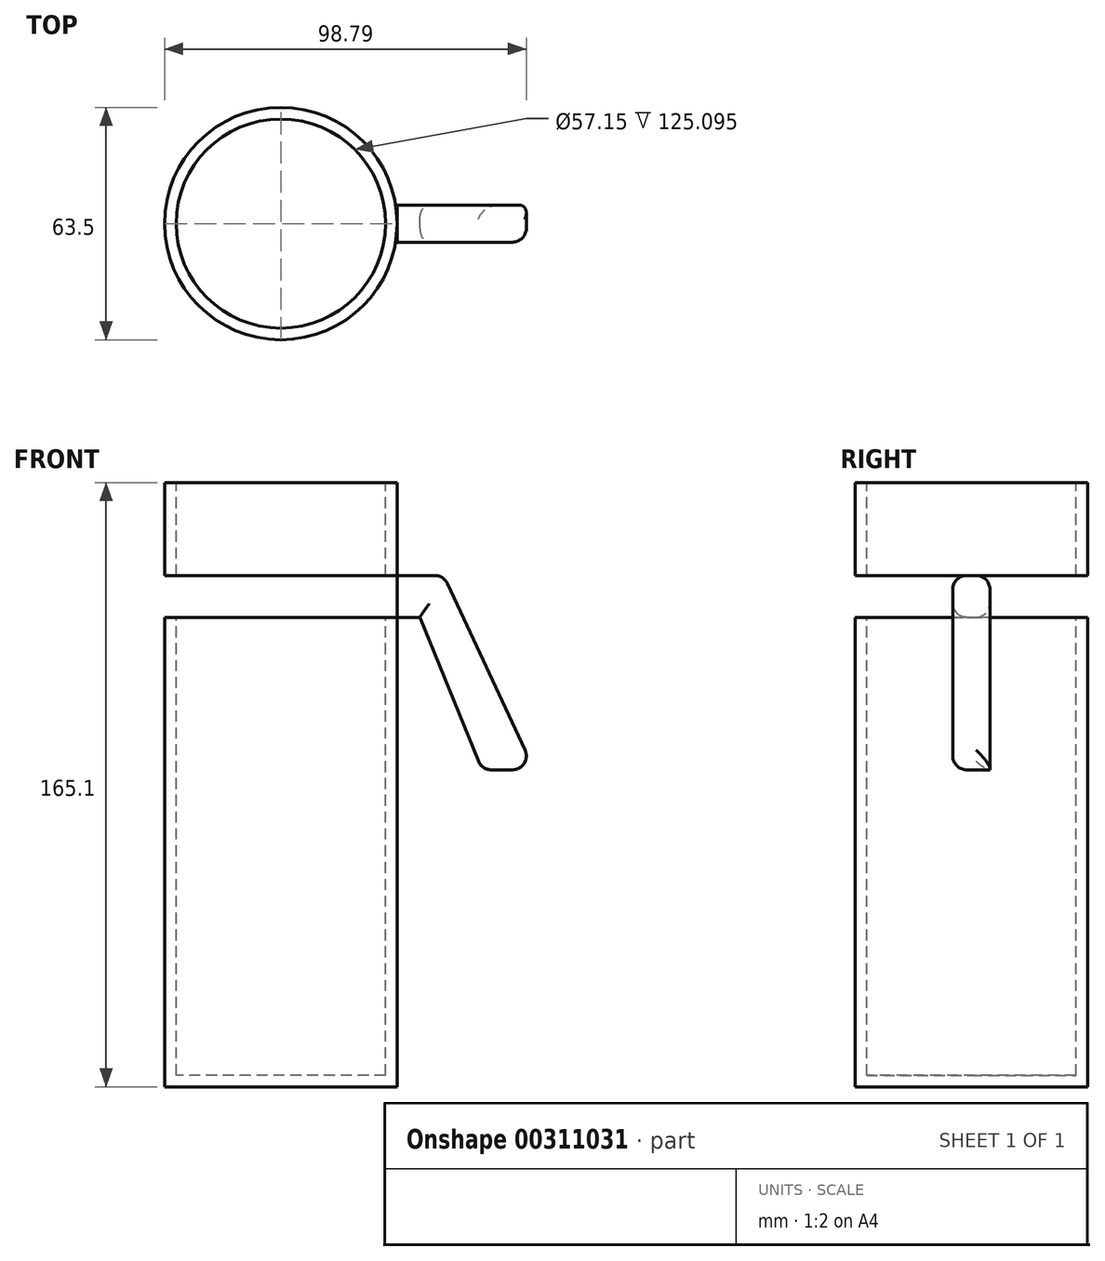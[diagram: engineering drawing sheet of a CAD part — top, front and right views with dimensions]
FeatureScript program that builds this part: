
annotation { "Feature Type Name" : "Feature", "Feature Type Description" : "" }
export const myFeature = defineFeature(function(context is Context, id is Id, definition is map)
    precondition{}
    {
        {
            var Q0;
            Q0=qCreatedBy(makeId("Front.planeOp"),FACE);
            var sketch = newSketch(context, id + "F0", { "sketchPlane" : qUnion([Q0])});
            skLineSegment(sketch, "E0", {"start": v(0, 227.4) * mm, "end": v(0, -63.53) * mm, "construction": true});
            skLineSegment(sketch, "E1", {"start": v(0, 118.52) * mm, "end": v(31.75, 118.52) * mm});
            skLineSegment(sketch, "E2", {"start": v(31.75, 118.52) * mm, "end": v(31.75, -46.58) * mm});
            skLineSegment(sketch, "E3", {"start": v(31.75, -46.58) * mm, "end": v(0, -46.58) * mm});
            skLineSegment(sketch, "E4", {"start": v(28.57, 118.52) * mm, "end": v(28.57, -43.4) * mm});
            skLineSegment(sketch, "E5", {"start": v(28.57, -43.4) * mm, "end": v(0, -43.4) * mm});
            skLineSegment(sketch, "E6", {"start": v(0, 118.52) * mm, "end": v(0, -46.58) * mm});
            skLineSegment(sketch, "E7", {"start": v(28.57, 93.12) * mm, "end": v(44.45, 93.12) * mm});
            skLineSegment(sketch, "E8", {"start": v(28.57, 81.7) * mm, "end": v(37.97, 81.7) * mm});
            skLineSegment(sketch, "E9", {"start": v(44.45, 93.12) * mm, "end": v(69.22, 40.02) * mm});
            skLineSegment(sketch, "E10", {"start": v(69.22, 40.02) * mm, "end": v(54.92, 40.02) * mm});
            skLineSegment(sketch, "E11", {"start": v(54.92, 40.02) * mm, "end": v(37.97, 81.7) * mm});
            skLineSegment(sketch, "E12", {"start": v(31.75, 93.12) * mm, "end": v(31.75, 81.7) * mm});
            skSolve(sketch);
        }
        {
            var Q0;
            {var subQ0=sQuery(id+"F0.wireOp",EDGE,"E2");var subQ1=sQuery(id+"F0.wireOp",EDGE,"E1");var subQ2=makeQuery(id+"F0.imprint","INTERSECT",VERTEX,{"derivedFrom":[subQ1,subQ0]});Q0=makeQuery(id+"F0.imprint","IMPRINT",FACE,{"disambiguationData":[TD([[makeQuery(id+"F0.imprint","IMPRINT",EDGE,{"disambiguationData":[TD([[subQ2,1.0]])],"derivedFrom":subQ1}),-1.0]])]});}
            var Q1;
            {var subQ5=sQuery(id+"F0.wireOp",EDGE,"E12");Q1=makeQuery(id+"F0.imprint","IMPRINT",FACE,{"disambiguationData":[TD([[makeQuery(id+"F0.imprint","IMPRINT",EDGE,{"derivedFrom":subQ5}),-1.0]])]});}
            var Q2;
            {var subQ4=sQuery(id+"F0.wireOp",EDGE,"E3");Q2=makeQuery(id+"F0.imprint","IMPRINT",FACE,{"disambiguationData":[TD([[makeQuery(id+"F0.imprint","IMPRINT",EDGE,{"derivedFrom":subQ4}),-1.0]])]});}
            var Q3;
            Q3=sQuery(id+"F0.wireOp",EDGE,"E6");
            revolve(context, id + "F1", {"entities" : qUnion([Q0, Q1, Q2]), "axis" : qUnion([Q3]), "revolveType" : RevolveType.FULL});
        }
        {
            var Q0;
            {var subQ5=sQuery(id+"F0.wireOp",EDGE,"E12");Q0=makeQuery(id+"F0.imprint","IMPRINT",FACE,{"disambiguationData":[TD([[makeQuery(id+"F0.imprint","IMPRINT",EDGE,{"derivedFrom":subQ5}),-1.0]])]});}
            var Q1;
            {var subQ0=sQuery(id+"F0.wireOp",EDGE,"E9");Q1=makeQuery(id+"F0.imprint","IMPRINT",FACE,{"disambiguationData":[TD([[makeQuery(id+"F0.imprint","IMPRINT",EDGE,{"derivedFrom":subQ0}),-1.0]])]});}
            extrude(context, id + "F2", {"entities" : qUnion([Q0, Q1]), "operationType" : NewBodyOperationType.ADD, "endBound" : BoundingType.SYMMETRIC, "depth" : 10.16 * mm});
        }
        {
            var Q0;
            Q0=makeQuery(id+"F2.opExtrude","CAP_EDGE",EDGE,{"disambiguationData":[OSD([sQuery(id+"F0.wireOp",EDGE,"E7")])],"isStart":false});
            var Q1;
            Q1=makeQuery(id+"F2.boolean.opBoolean","INTERSECT",EDGE,{"derivedFrom":[makeQuery(id+"F1.opRevolve","SWEPT_FACE",FACE,{"disambiguationData":[OSD([sQuery(id+"F0.wireOp",EDGE,"E2"),sQuery(id+"F0.wireOp",EDGE,"E12")])]}),makeQuery(id+"F2.opExtrude","SWEPT_FACE",FACE,{"disambiguationData":[OSD([sQuery(id+"F0.wireOp",EDGE,"E7")])]})]});
            var Q2;
            Q2=makeQuery(id+"F2.opExtrude","CAP_EDGE",EDGE,{"disambiguationData":[OSD([sQuery(id+"F0.wireOp",EDGE,"E7")])],"isStart":true});
            var Q3;
            Q3=makeQuery(id+"F2.boolean.opBoolean","INTERSECT",EDGE,{"derivedFrom":[makeQuery(id+"F1.opRevolve","SWEPT_FACE",FACE,{"disambiguationData":[OSD([sQuery(id+"F0.wireOp",EDGE,"E2"),sQuery(id+"F0.wireOp",EDGE,"E12")])]}),makeQuery(id+"F2.opExtrude","CAP_FACE",FACE,{"disambiguationData":[OSD([sQuery(id+"F0.wireOp",EDGE,"E4"),sQuery(id+"F0.wireOp",EDGE,"E7"),sQuery(id+"F0.wireOp",EDGE,"E8"),sQuery(id+"F0.wireOp",EDGE,"E9"),sQuery(id+"F0.wireOp",EDGE,"E10"),sQuery(id+"F0.wireOp",EDGE,"E11")])],"isStart":false})]});
            var Q4;
            Q4=makeQuery(id+"F2.opExtrude","CAP_EDGE",EDGE,{"disambiguationData":[OSD([sQuery(id+"F0.wireOp",EDGE,"E8")])],"isStart":false});
            var Q5;
            Q5=makeQuery(id+"F2.boolean.opBoolean","INTERSECT",EDGE,{"derivedFrom":[makeQuery(id+"F1.opRevolve","SWEPT_FACE",FACE,{"disambiguationData":[OSD([sQuery(id+"F0.wireOp",EDGE,"E2"),sQuery(id+"F0.wireOp",EDGE,"E12")])]}),makeQuery(id+"F2.opExtrude","CAP_FACE",FACE,{"disambiguationData":[OSD([sQuery(id+"F0.wireOp",EDGE,"E4"),sQuery(id+"F0.wireOp",EDGE,"E7"),sQuery(id+"F0.wireOp",EDGE,"E8"),sQuery(id+"F0.wireOp",EDGE,"E9"),sQuery(id+"F0.wireOp",EDGE,"E10"),sQuery(id+"F0.wireOp",EDGE,"E11")])],"isStart":true})]});
            var Q6;
            Q6=makeQuery(id+"F2.opExtrude","CAP_EDGE",EDGE,{"disambiguationData":[OSD([sQuery(id+"F0.wireOp",EDGE,"E8")])],"isStart":true});
            var Q7;
            Q7=makeQuery(id+"F2.opExtrude","CAP_EDGE",EDGE,{"disambiguationData":[OSD([sQuery(id+"F0.wireOp",EDGE,"E11")])],"isStart":true});
            var Q8;
            Q8=makeQuery(id+"F2.opExtrude","CAP_EDGE",EDGE,{"disambiguationData":[OSD([sQuery(id+"F0.wireOp",EDGE,"E9")])],"isStart":true});
            var Q9;
            Q9=makeQuery(id+"F2.opExtrude","CAP_EDGE",EDGE,{"disambiguationData":[OSD([sQuery(id+"F0.wireOp",EDGE,"E9")])],"isStart":false});
            var Q10;
            Q10=makeQuery(id+"F2.opExtrude","CAP_EDGE",EDGE,{"disambiguationData":[OSD([sQuery(id+"F0.wireOp",EDGE,"E11")])],"isStart":false});
            var Q11;
            Q11=makeQuery(id+"F2.opExtrude","SWEPT_EDGE",EDGE,{"disambiguationData":[OSD([sQuery(id+"F0.wireOp",EDGE,"E9"),sQuery(id+"F0.wireOp",EDGE,"E10")])]});
            var Q12;
            Q12=makeQuery(id+"F2.opExtrude","SWEPT_EDGE",EDGE,{"disambiguationData":[OSD([sQuery(id+"F0.wireOp",EDGE,"E10"),sQuery(id+"F0.wireOp",EDGE,"E11")])]});
            var Q13;
            Q13=makeQuery(id+"F2.opExtrude","CAP_EDGE",EDGE,{"disambiguationData":[OSD([sQuery(id+"F0.wireOp",EDGE,"E10")])],"isStart":false});
            var Q14;
            Q14=makeQuery(id+"F2.opExtrude","SWEPT_EDGE",EDGE,{"disambiguationData":[OSD([sQuery(id+"F0.wireOp",EDGE,"E7"),sQuery(id+"F0.wireOp",EDGE,"E9")])]});
            fillet(context, id + "F3", {"entities" : qUnion([Q0, Q1, Q2, Q3, Q4, Q5, Q6, Q7, Q8, Q9, Q10, Q11, Q12, Q13, Q14]), "radius" : 3.8 * mm, "tangentPropagation" : true, "allowEdgeOverflow" : false});
        }
    });
